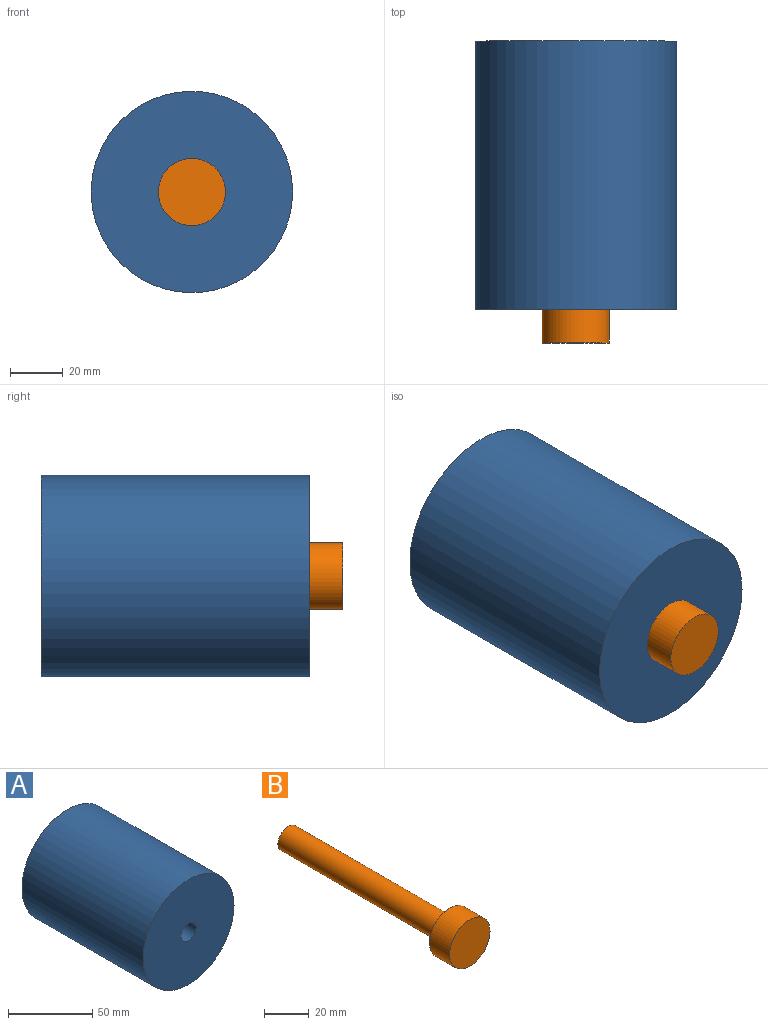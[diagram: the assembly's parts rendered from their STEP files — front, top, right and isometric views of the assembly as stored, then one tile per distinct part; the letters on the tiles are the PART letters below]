
ASSEMBLY  parts=2 mates=1
PART A: 4 faces, bbox 76.2x101.6x76.2 mm
  f0: cylinder r=6.35mm len=101.6mm, axis (0,1,0), area 4053.7mm2, adj f2,f3
  f1: cylinder r=38.1mm len=101.6mm, axis (0,1,0), area 24322mm2, adj f2,f3
  f2: plane 76.2x76.2mm, normal (0,-1,0), area 4433.7mm2, adj f0,f1
  f3: plane 76.2x76.2mm, normal (0,1,0), area 4433.7mm2, adj f0,f1
PART B: 5 faces, bbox 25.4x114.3x25.4 mm
  f0: cylinder r=6.35mm len=101.6mm, axis (0,1,0), area 4053.7mm2, adj f1,f4
  f1: plane 12.7x12.7mm, normal (0,1,0), area 126.7mm2, adj f0
  f2: plane 25.4x25.4mm, normal (0,-1,0), area 506.7mm2, adj f3
  f3: cylinder r=12.7mm len=25.4mm, axis (0,1,0), area 1013.4mm2, adj f2,f4
  f4: plane 25.4x25.4mm, normal (0,1,0), area 380mm2, adj f0,f3
PLACE A t=(133.72,-1.05,-4.34)mm fixed
PLACE B rot(axis=(0,1,0),57.3deg) t=(128.37,-55.15,30.02)mm
MATE revolute B.f0 <-> A.f0  axis (0,1,0) through (133.72,-1.05,33.45)mm
